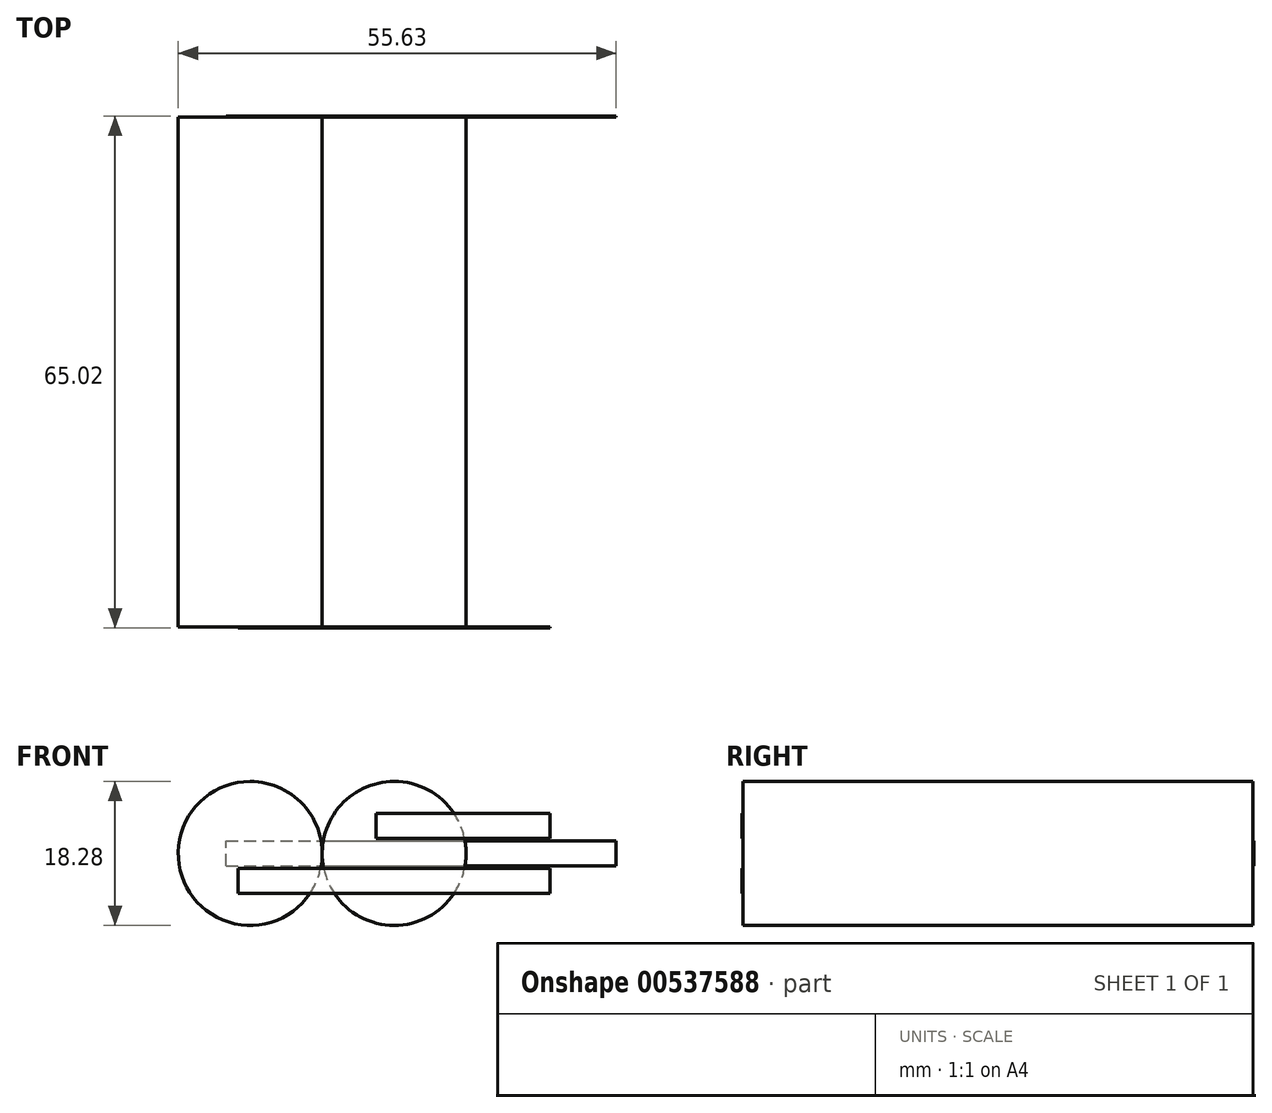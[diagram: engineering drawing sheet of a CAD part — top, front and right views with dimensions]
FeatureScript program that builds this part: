
annotation { "Feature Type Name" : "Feature", "Feature Type Description" : "" }
export const myFeature = defineFeature(function(context is Context, id is Id, definition is map)
    precondition{}
    {
        {
            var Q0;
            Q0=qCreatedBy(makeId("Front.planeOp"),FACE);
            var sketch = newSketch(context, id + "F0", { "sketchPlane" : qUnion([Q0])});
            skCircle(sketch, "E0", {"center": v(-9.14, 0) * mm, "radius": 9.14 * mm});
            skCircle(sketch, "E1", {"center": v(9.14, 0) * mm, "radius": 9.14 * mm});
            skSolve(sketch);
        }
        {
            var Q0;
            Q0 = qSketchRegion(id + "F0", true);
            extrude(context, id + "F1", {"entities" : qUnion([Q0]), "endBound" : BoundingType.SYMMETRIC, "depth" : 64.77 * mm, "offsetDistance" : 25.4 * mm});
        }
        {
            var Q0;
            Q0=makeQuery(id+"F1.opExtrude","CAP_FACE",FACE,{"disambiguationData":[OSD([sQuery(id+"F0.wireOp",EDGE,"E1")])],"isStart":true});
            var sketch = newSketch(context, id + "F2", { "sketchPlane" : qUnion([Q0])});
            skLineSegment(sketch, "E2.bottom", {"start": v(-12.2, 1.59) * mm, "end": v(37.34, 1.59) * mm});
            skLineSegment(sketch, "E2.top", {"start": v(-12.2, -1.59) * mm, "end": v(37.34, -1.59) * mm});
            skLineSegment(sketch, "E2.left", {"start": v(-12.2, 1.59) * mm, "end": v(-12.2, -1.59) * mm});
            skLineSegment(sketch, "E2.right", {"start": v(37.34, 1.59) * mm, "end": v(37.34, -1.59) * mm});
            skLineSegment(sketch, "E3", {"start": v(41.1, 0) * mm, "end": v(-7.41, 0) * mm, "construction": true});
            skSolve(sketch);
        }
        {
            var Q0;
            Q0 = qSketchRegion(id + "F2", true);
            extrude(context, id + "F3", {"entities" : qUnion([Q0]), "depth" : 0.13 * mm, "offsetDistance" : 25.4 * mm});
        }
        {
            var Q0;
            Q0=makeQuery(id+"F1.opExtrude","CAP_FACE",FACE,{"disambiguationData":[OSD([sQuery(id+"F0.wireOp",EDGE,"E1")])],"isStart":false});
            var sketch = newSketch(context, id + "F4", { "sketchPlane" : qUnion([Q0])});
            skLineSegment(sketch, "E4.bottom", {"start": v(10.67, 5.08) * mm, "end": v(-28.96, 5.08) * mm});
            skLineSegment(sketch, "E4.top", {"start": v(10.67, 1.9) * mm, "end": v(-28.96, 1.9) * mm});
            skLineSegment(sketch, "E4.left", {"start": v(10.67, 5.08) * mm, "end": v(10.67, 1.9) * mm});
            skLineSegment(sketch, "E4.right", {"start": v(-28.96, 5.08) * mm, "end": v(-28.96, 1.9) * mm});
            skLineSegment(sketch, "E5.bottom", {"start": v(-6.86, -1.9) * mm, "end": v(-28.96, -1.9) * mm});
            skLineSegment(sketch, "E5.top", {"start": v(-6.86, -5.08) * mm, "end": v(-28.96, -5.08) * mm});
            skLineSegment(sketch, "E5.left", {"start": v(-6.86, -1.9) * mm, "end": v(-6.86, -5.08) * mm});
            skLineSegment(sketch, "E5.right", {"start": v(-28.96, -1.9) * mm, "end": v(-28.96, -5.08) * mm});
            skLineSegment(sketch, "E6", {"start": v(-28.96, 3.5) * mm, "end": v(10.67, 3.5) * mm, "construction": true});
            skLineSegment(sketch, "E7", {"start": v(-28.96, -3.5) * mm, "end": v(-6.86, -3.5) * mm, "construction": true});
            skSolve(sketch);
        }
        {
            var Q0;
            Q0 = qSketchRegion(id + "F4", true);
            extrude(context, id + "F5", {"entities" : qUnion([Q0]), "depth" : 0.13 * mm, "offsetDistance" : 25.4 * mm});
        }
        {
            var Q0;
            Q0=makeQuery(id+"F1.opExtrude","SWEPT_BODY",BODY,{"disambiguationData":[OSD([sQuery(id+"F0.wireOp",EDGE,"E0")])]});
            var Q1;
            Q1=makeQuery(id+"F1.opExtrude","SWEPT_BODY",BODY,{"disambiguationData":[OSD([sQuery(id+"F0.wireOp",EDGE,"E1")])]});
            var Q2;
            Q2=makeQuery(id+"F3.opExtrude","SWEPT_BODY",BODY,{"disambiguationData":[OSD([sQuery(id+"F2.wireOp",EDGE,"E2.bottom"),sQuery(id+"F2.wireOp",EDGE,"E2.top"),sQuery(id+"F2.wireOp",EDGE,"E2.left"),sQuery(id+"F2.wireOp",EDGE,"E2.right")])]});
            var Q3;
            Q3=makeQuery(id+"F5.opExtrude","SWEPT_BODY",BODY,{"disambiguationData":[OSD([sQuery(id+"F4.wireOp",EDGE,"E4.bottom"),sQuery(id+"F4.wireOp",EDGE,"E4.top"),sQuery(id+"F4.wireOp",EDGE,"E4.left"),sQuery(id+"F4.wireOp",EDGE,"E4.right")])]});
            var Q4;
            Q4=makeQuery(id+"F5.opExtrude","SWEPT_BODY",BODY,{"disambiguationData":[OSD([sQuery(id+"F4.wireOp",EDGE,"E5.bottom"),sQuery(id+"F4.wireOp",EDGE,"E5.top"),sQuery(id+"F4.wireOp",EDGE,"E5.left"),sQuery(id+"F4.wireOp",EDGE,"E5.right")])]});
            var Q5;
            Q5=makeQuery(id+"F1.opExtrude","SWEPT_FACE",FACE,{"disambiguationData":[OSD([sQuery(id+"F0.wireOp",EDGE,"E1")])]});
            transform(context, id + "F6", {"entities" : qUnion([Q0, Q1, Q2, Q3, Q4]), "transformType" : TransformType.ROTATION, "transformAxis" : qUnion([Q5]), "angle" : 180 * degree, "makeCopy" : false});
        }
    });
